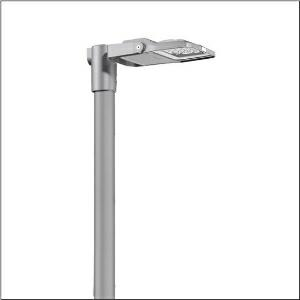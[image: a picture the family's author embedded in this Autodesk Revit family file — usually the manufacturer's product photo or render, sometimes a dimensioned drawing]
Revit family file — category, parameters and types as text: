
# Revit family: floodlight_fl_21_iq_micro___pl64_5xa7762a2e3a_859a
name_source: partatom
category: Lighting Fixtures
units: mm (PartAtom-declared; Revit-internal decimal feet)

## family parameters
Cut with Voids When Loaded = No
Host = Face
Light Source = No
Part Type = Normal
Room Calculation Point = No
Round Connector Dimension = Use Diameter
Shared = No

## types (1)
- --- (1 x LED, 2870 lm, 23.1 W, 3000K)
    Apparent Load = 23 VA
    CIE Flux Codes = 28 80 98 100 100
    Color Rendering = 70
    Color Temperature = 3000K
    Default Elevation = 1800 mm
    Description = Floodlight FL 21 iQ micro, floodlight, primary light control with lens, of PMMA, primary optical cover: protective disc, of toughened safety glass, transparent, light distribution: PL64, light emission: direct distribution, installation type: surface-mounted, lamps: LED, High Power LED, rated values: 2.870lm | 23,1W | 124,2lm/W (begin service life); end service life: 2.870lm | 23,8W; at 50% lumin. flux: 1.435lm | 11W | 130,5lm/W, colour temperature: 3000K, colour rendering: CRI > 70, light colour: 730, light setting 1 begin service life: 100% | 2.870lm | 23,1W | 124,2lm/W | 3.000K, light setting 1 end service life: 23,8W, further light settings possible, control: Auto-Match, Temp-Guard, Night-Set, Smart-Wire, Desk-Remote (wireless, voltage-free reading and setting of iQ features in the workshop via application-optimized NFC function/RFID function), optimised constant luminous flux control (CLO 2.0), Street-Remote, pre-setting: linear dimming characteristic, with terminal, 6-pole, mains connection: 220..240V, AC, 50/60Hz, luminaire housing, of diecast aluminium, powder-coated, SITECO metallic grey (DB 702S), corrosivity category C5 mid according to DIN EN ISO 12944suitable for swimming poolschlorine-resistant, sealing non-destructively replaceable, please order mast flange separately, mast bracket, of steel, galvanised, powder-coated, SITECO metallic grey (DB 702S), protection rating (complete): IP66, insulation class (complete): insulation class II (safety insulation), certification: CE, ENEC, VDE, protection symbol: D, impact resistance: IK07, permissible operating ambient temperature: -40..+40°C, permissible operating ambient temperature for outdoor applications: -40..+50°C, standard: DIN EN 12944, LABS conformity tested according to VDMA 24364:2018-05, packaging unit: 1 piece

Light Distribution: PL64
    Height = 65 mm
    Lamp = 1 x LED
    Lamp Light Flux = 2870 lm
    Lamp Power = 23.1 W
    Lamp count = 1
    Length = 312 mm
    Luminous efficacy = 124 lm/W
    Manufacturer = Siteco
    ModVariant = No
    Model = 5XA7762A2E3A
    Number of Poles = 1
    OnlyDefault = Yes
    Power Factor = 1
    Product Name = Floodlight FL 21 iQ micro | PL64
    Product group = floodlight | pylon annexe
    ProductGroupID = 6201
    Protection Class = Protection class II
    Protection Degree = IP 66
    RLX_Detail_Level = 1
    RLX_Emergency_Light_Flux = 0 lm
    RLX_Emergency_Type = 0
    RLX_Emergency_Type_DB = No
    RlxData = <blob elided: 102065 chars, md5=280244bd>
    Socket = socket
    Standby Power = 0 W
    System Light Flux = 2870 lm
    System Power = 23 W
    Type Comments = factory setting: luminous flux: 100 % | dim-lin: 254 | 455 mA
    Type Image = l_1007121.jpg
    URL = http://relux.com
    VarID = @adj_179345
    Voltage = 0 V
    Weight = 0.00 kg
    Width = 230 mm

## geometry (parser evidence)
native form markers: Blend x4, Sweep x11
no freeform markers — native parametric forms only
